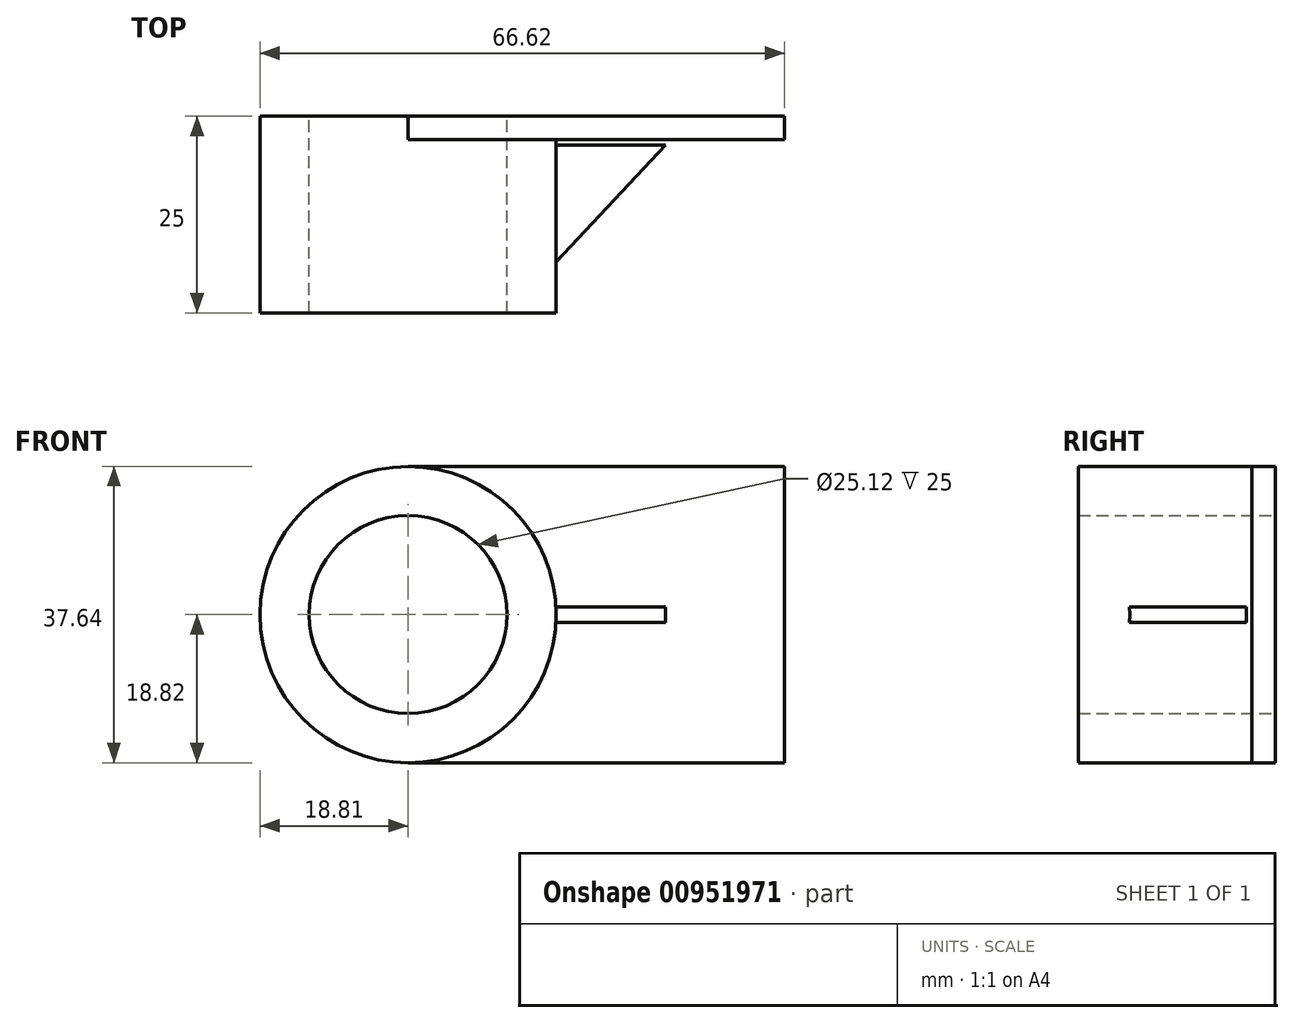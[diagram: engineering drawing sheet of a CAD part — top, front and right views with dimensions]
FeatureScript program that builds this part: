
annotation { "Feature Type Name" : "Feature", "Feature Type Description" : "" }
export const myFeature = defineFeature(function(context is Context, id is Id, definition is map)
    precondition{}
    {
        {
            var Q0;
            Q0=qCreatedBy(makeId("Front.planeOp"),FACE);
            var sketch = newSketch(context, id + "F0", { "sketchPlane" : qUnion([Q0])});
            skCircle(sketch, "E0", {"center": v(0, 0) * mm, "radius": 12.56 * mm});
            skCircle(sketch, "E1", {"center": v(0, 0) * mm, "radius": 18.81 * mm});
            skSolve(sketch);
        }
        {
            var Q0;
            Q0=makeQuery(id+"F0.imprint","IMPRINT",FACE,{"disambiguationData":[TD([[makeQuery(id+"F0.imprint","IMPRINT",EDGE,{"derivedFrom":sQuery(id+"F0.wireOp",EDGE,"E0")}),-1.0]])]});
            extrude(context, id + "F1", {"entities" : qUnion([Q0]), "depth" : 25 * mm, "offsetDistance" : 25 * mm});
        }
        {
            var Q0;
            Q0=qCreatedBy(makeId("Front.planeOp"),FACE);
            var sketch = newSketch(context, id + "F2", { "sketchPlane" : qUnion([Q0])});
            skLineSegment(sketch, "E2.bottom", {"start": v(0, 18.82) * mm, "end": v(47.81, 18.82) * mm});
            skLineSegment(sketch, "E2.top", {"start": v(0, -18.79) * mm, "end": v(47.81, -18.79) * mm});
            skLineSegment(sketch, "E2.left", {"start": v(0, 18.82) * mm, "end": v(0, -18.79) * mm});
            skLineSegment(sketch, "E2.right", {"start": v(47.81, 18.82) * mm, "end": v(47.81, -18.79) * mm});
            skSolve(sketch);
        }
        {
            var Q0;
            Q0=makeQuery(id+"F2.imprint","IMPRINT",FACE,{"disambiguationData":[TD([[makeQuery(id+"F2.imprint","IMPRINT",EDGE,{"derivedFrom":sQuery(id+"F2.wireOp",EDGE,"E2.bottom")}),-1.0]])]});
            extrude(context, id + "F3", {"entities" : qUnion([Q0]), "operationType" : NewBodyOperationType.ADD, "depth" : 3 * mm, "offsetDistance" : 25 * mm});
        }
        {
            var Q0;
            Q0=qCreatedBy(makeId("Top.planeOp"),FACE);
            var sketch = newSketch(context, id + "F4", { "sketchPlane" : qUnion([Q0])});
            skLineSegment(sketch, "E3", {"start": v(18.8, -18.5) * mm, "end": v(32.71, -3.7) * mm});
            skLineSegment(sketch, "E4", {"start": v(32.71, -3.7) * mm, "end": v(18.5, -3.7) * mm});
            skLineSegment(sketch, "E5", {"start": v(18.5, -3.7) * mm, "end": v(18.8, -18.5) * mm});
            skSolve(sketch);
        }
        {
            var Q0;
            Q0=makeQuery(id+"F4.imprint","IMPRINT",FACE,{"disambiguationData":[TD([[makeQuery(id+"F4.imprint","IMPRINT",EDGE,{"derivedFrom":sQuery(id+"F4.wireOp",EDGE,"E3")}),1.0]])]});
            extrude(context, id + "F5", {"entities" : qUnion([Q0]), "operationType" : NewBodyOperationType.ADD, "depth" : 1 * mm, "offsetDistance" : 25 * mm});
        }
        {
            var Q0;
            Q0=makeQuery(id+"F1.opExtrude","SWEPT_BODY",BODY,{"disambiguationData":[OSD([sQuery(id+"F0.wireOp",EDGE,"E0"),sQuery(id+"F0.wireOp",EDGE,"E1")])]});
            var Q1;
            Q1=makeQuery(id+"F5.opExtrude","CAP_FACE",FACE,{"disambiguationData":[OSD([sQuery(id+"F4.wireOp",EDGE,"E3"),sQuery(id+"F4.wireOp",EDGE,"E4"),sQuery(id+"F4.wireOp",EDGE,"E5")])],"isStart":true});
            mirror(context, id + "F6", {"operationType" : NewBodyOperationType.ADD, "entities" : qUnion([Q0]), "mirrorPlane" : qUnion([Q1])});
        }
        {
            var Q0;
            {var subQ0=sQuery(id+"F2.wireOp",EDGE,"E2.left");Q0=makeQuery(id+"F3.boolean.opBoolean","SPLIT",FACE,{"disambiguationData":[TD([makeQuery(id+"F1.opExtrude","SWEPT_FACE",FACE,{"disambiguationData":[OSD([sQuery(id+"F0.wireOp",EDGE,"E0")])]})])],"derivedFrom":makeQuery(id+"F3.opExtrude","CAP_FACE",FACE,{"disambiguationData":[OSD([sQuery(id+"F2.wireOp",EDGE,"E2.bottom"),sQuery(id+"F2.wireOp",EDGE,"E2.top"),subQ0,sQuery(id+"F2.wireOp",EDGE,"E2.right")])],"isStart":false})});}
            extrude(context, id + "F7", {"entities" : qUnion([Q0]), "operationType" : NewBodyOperationType.REMOVE, "oppositeDirection" : true, "depth" : 25 * mm, "offsetDistance" : 25 * mm});
        }
    });
